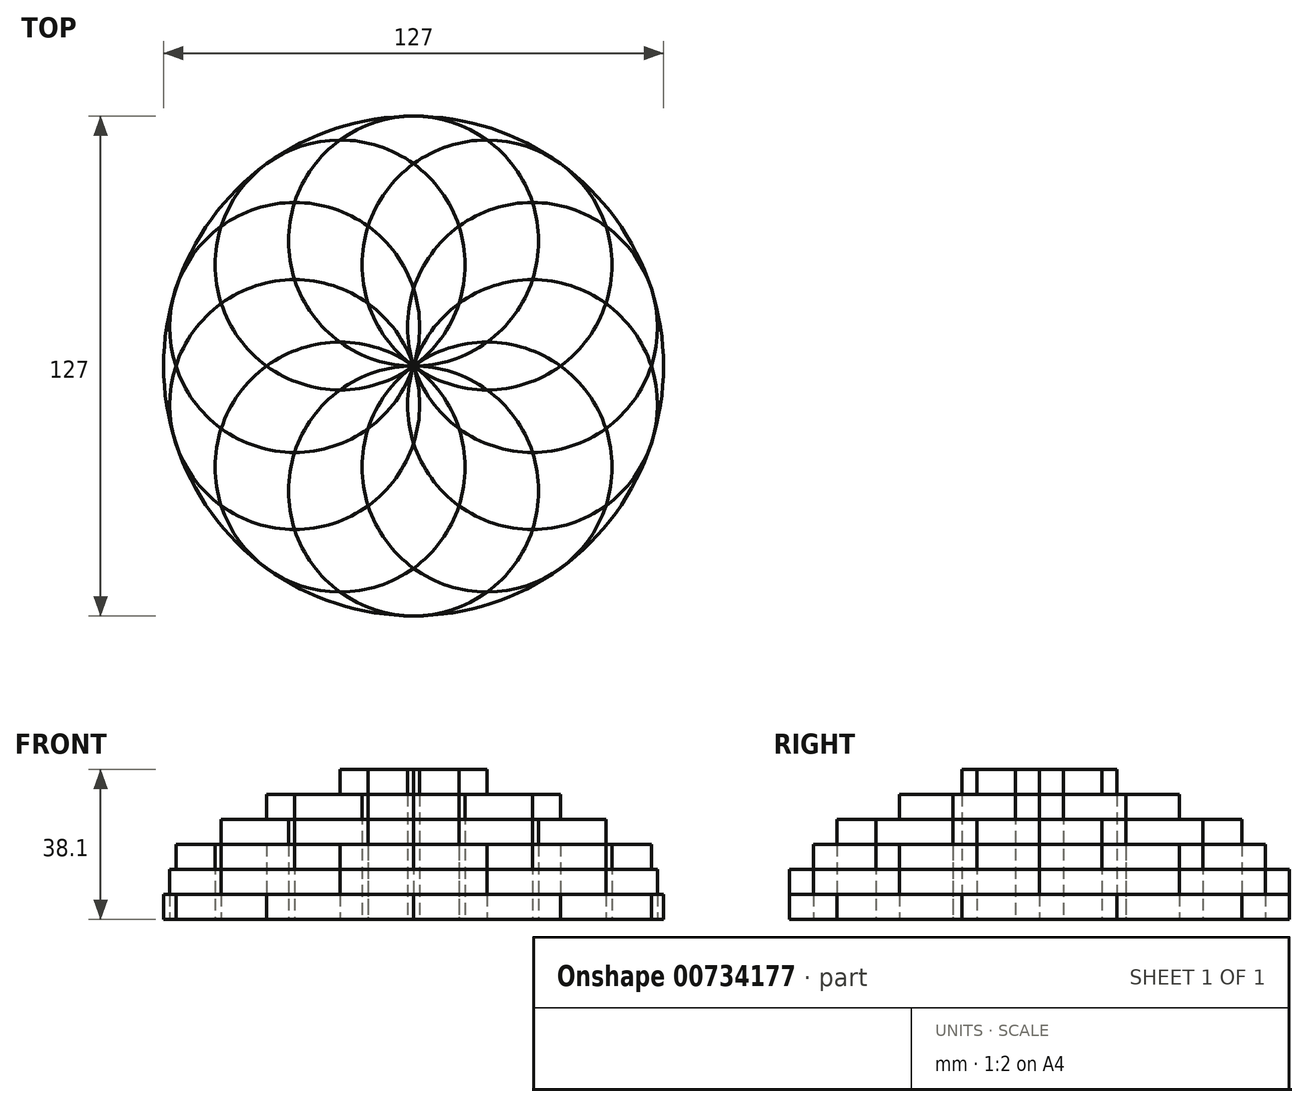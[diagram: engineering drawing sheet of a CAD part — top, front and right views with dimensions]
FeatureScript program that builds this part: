
annotation { "Feature Type Name" : "Feature", "Feature Type Description" : "" }
export const myFeature = defineFeature(function(context is Context, id is Id, definition is map)
    precondition{}
    {
        {
            var Q0;
            Q0=qCreatedBy(makeId("Top.planeOp"),FACE);
            var sketch = newSketch(context, id + "F0", { "sketchPlane" : qUnion([Q0])});
            skCircle(sketch, "E0", {"center": v(0, 0) * mm, "radius": 63.5 * mm});
            skCircle(sketch, "E1", {"center": v(0, 31.75) * mm, "radius": 31.75 * mm});
            skCircle(sketch, "E2.1.0", {"center": v(-18.66, 25.69) * mm, "radius": 31.75 * mm});
            skCircle(sketch, "E2.2.0", {"center": v(-30.2, 9.81) * mm, "radius": 31.75 * mm});
            skCircle(sketch, "E2.3.0", {"center": v(-30.2, -9.81) * mm, "radius": 31.75 * mm});
            skCircle(sketch, "E2.4.0", {"center": v(-18.66, -25.69) * mm, "radius": 31.75 * mm});
            skCircle(sketch, "E2.5.0", {"center": v(0, -31.75) * mm, "radius": 31.75 * mm});
            skCircle(sketch, "E2.6.0", {"center": v(18.66, -25.69) * mm, "radius": 31.75 * mm});
            skCircle(sketch, "E2.7.0", {"center": v(30.2, -9.81) * mm, "radius": 31.75 * mm});
            skCircle(sketch, "E2.8.0", {"center": v(30.2, 9.81) * mm, "radius": 31.75 * mm});
            skCircle(sketch, "E2.9.0", {"center": v(18.66, 25.69) * mm, "radius": 31.75 * mm});
            skSolve(sketch);
        }
        {
            var Q0;
            {var subQ0=sQuery(id+"F0.wireOp",EDGE,"E1");var subQ1=sQuery(id+"F0.wireOp",EDGE,"E0");var subQ2=makeQuery(id+"F0.imprint","INTERSECT",VERTEX,{"derivedFrom":[subQ1,subQ0]});Q0=makeQuery(id+"F0.imprint","IMPRINT",FACE,{"disambiguationData":[TD([[makeQuery(id+"F0.imprint","IMPRINT",EDGE,{"disambiguationData":[TD([[subQ2,-1.0]])],"derivedFrom":subQ1}),1.0]])]});}
            var Q1;
            {var subQ0=sQuery(id+"F0.wireOp",EDGE,"E2.1.0");var subQ1=sQuery(id+"F0.wireOp",EDGE,"E0");var subQ2=makeQuery(id+"F0.imprint","INTERSECT",VERTEX,{"derivedFrom":[subQ1,subQ0]});Q1=makeQuery(id+"F0.imprint","IMPRINT",FACE,{"disambiguationData":[TD([[makeQuery(id+"F0.imprint","IMPRINT",EDGE,{"disambiguationData":[TD([[subQ2,-1.0]])],"derivedFrom":subQ1}),1.0]])]});}
            var Q2;
            {var subQ0=sQuery(id+"F0.wireOp",EDGE,"E2.2.0");var subQ1=sQuery(id+"F0.wireOp",EDGE,"E0");var subQ2=makeQuery(id+"F0.imprint","INTERSECT",VERTEX,{"derivedFrom":[subQ1,subQ0]});Q2=makeQuery(id+"F0.imprint","IMPRINT",FACE,{"disambiguationData":[TD([[makeQuery(id+"F0.imprint","IMPRINT",EDGE,{"disambiguationData":[TD([[subQ2,-1.0]])],"derivedFrom":subQ1}),1.0]])]});}
            var Q3;
            {var subQ0=sQuery(id+"F0.wireOp",EDGE,"E2.3.0");var subQ1=sQuery(id+"F0.wireOp",EDGE,"E0");var subQ2=makeQuery(id+"F0.imprint","INTERSECT",VERTEX,{"derivedFrom":[subQ1,subQ0]});Q3=makeQuery(id+"F0.imprint","IMPRINT",FACE,{"disambiguationData":[TD([[makeQuery(id+"F0.imprint","IMPRINT",EDGE,{"disambiguationData":[TD([[subQ2,-1.0]])],"derivedFrom":subQ1}),1.0]])]});}
            var Q4;
            {var subQ0=sQuery(id+"F0.wireOp",EDGE,"E2.4.0");var subQ1=sQuery(id+"F0.wireOp",EDGE,"E0");var subQ2=makeQuery(id+"F0.imprint","INTERSECT",VERTEX,{"derivedFrom":[subQ1,subQ0]});Q4=makeQuery(id+"F0.imprint","IMPRINT",FACE,{"disambiguationData":[TD([[makeQuery(id+"F0.imprint","IMPRINT",EDGE,{"disambiguationData":[TD([[subQ2,-1.0]])],"derivedFrom":subQ1}),1.0]])]});}
            var Q5;
            {var subQ0=sQuery(id+"F0.wireOp",EDGE,"E2.5.0");var subQ1=sQuery(id+"F0.wireOp",EDGE,"E0");var subQ2=makeQuery(id+"F0.imprint","INTERSECT",VERTEX,{"derivedFrom":[subQ1,subQ0]});Q5=makeQuery(id+"F0.imprint","IMPRINT",FACE,{"disambiguationData":[TD([[makeQuery(id+"F0.imprint","IMPRINT",EDGE,{"disambiguationData":[TD([[subQ2,-1.0]])],"derivedFrom":subQ1}),1.0]])]});}
            var Q6;
            {var subQ0=sQuery(id+"F0.wireOp",EDGE,"E2.6.0");var subQ1=sQuery(id+"F0.wireOp",EDGE,"E0");var subQ2=makeQuery(id+"F0.imprint","INTERSECT",VERTEX,{"derivedFrom":[subQ1,subQ0]});Q6=makeQuery(id+"F0.imprint","IMPRINT",FACE,{"disambiguationData":[TD([[makeQuery(id+"F0.imprint","IMPRINT",EDGE,{"disambiguationData":[TD([[subQ2,-1.0]])],"derivedFrom":subQ1}),1.0]])]});}
            var Q7;
            {var subQ0=sQuery(id+"F0.wireOp",EDGE,"E2.9.0");var subQ1=sQuery(id+"F0.wireOp",EDGE,"E0");var subQ2=makeQuery(id+"F0.imprint","INTERSECT",VERTEX,{"derivedFrom":[subQ1,subQ0]});Q7=makeQuery(id+"F0.imprint","IMPRINT",FACE,{"disambiguationData":[TD([[makeQuery(id+"F0.imprint","IMPRINT",EDGE,{"disambiguationData":[TD([[subQ2,-1.0]])],"derivedFrom":subQ1}),1.0]])]});}
            var Q8;
            {var subQ0=sQuery(id+"F0.wireOp",EDGE,"E2.9.0");var subQ1=sQuery(id+"F0.wireOp",EDGE,"E0");var subQ2=makeQuery(id+"F0.imprint","INTERSECT",VERTEX,{"derivedFrom":[subQ1,subQ0]});Q8=makeQuery(id+"F0.imprint","IMPRINT",FACE,{"disambiguationData":[TD([[makeQuery(id+"F0.imprint","IMPRINT",EDGE,{"disambiguationData":[TD([[subQ2,1.0]])],"derivedFrom":subQ1}),1.0]])]});}
            var Q9;
            {var subQ0=sQuery(id+"F0.wireOp",EDGE,"E2.8.0");var subQ1=sQuery(id+"F0.wireOp",EDGE,"E0");var subQ2=makeQuery(id+"F0.imprint","INTERSECT",VERTEX,{"derivedFrom":[subQ1,subQ0]});Q9=makeQuery(id+"F0.imprint","IMPRINT",FACE,{"disambiguationData":[TD([[makeQuery(id+"F0.imprint","IMPRINT",EDGE,{"disambiguationData":[TD([[subQ2,1.0]])],"derivedFrom":subQ1}),1.0]])]});}
            extrude(context, id + "F1", {"entities" : qUnion([Q0, Q1, Q2, Q3, Q4, Q5, Q6, Q7, Q8, Q9]), "depth" : 6.35 * mm, "offsetDistance" : 25.4 * mm});
        }
        {
            var Q0;
            {var subQ0=sQuery(id+"F0.wireOp",EDGE,"E2.1.0");var subQ1=sQuery(id+"F0.wireOp",EDGE,"E1");var subQ2=makeQuery(id+"F0.imprint","INTERSECT",VERTEX,{"derivedFrom":[subQ1,subQ0]});Q0=makeQuery(id+"F0.imprint","IMPRINT",FACE,{"disambiguationData":[TD([[makeQuery(id+"F0.imprint","IMPRINT",EDGE,{"disambiguationData":[TD([[subQ2,-1.0]])],"derivedFrom":subQ1}),-1.0]])]});}
            var Q1;
            {var subQ0=sQuery(id+"F0.wireOp",EDGE,"E1");var subQ1=makeQuery(id+"F0.imprint","INTERSECT",VERTEX,{"derivedFrom":[sQuery(id+"F0.wireOp",EDGE,"E0"),subQ0]});Q1=makeQuery(id+"F0.imprint","IMPRINT",FACE,{"disambiguationData":[TD([[makeQuery(id+"F0.imprint","IMPRINT",EDGE,{"disambiguationData":[TD([[subQ1,1.0]])],"derivedFrom":subQ0}),1.0]])]});}
            var Q2;
            {var subQ0=sQuery(id+"F0.wireOp",EDGE,"E2.9.0");var subQ1=sQuery(id+"F0.wireOp",EDGE,"E1");var subQ2=makeQuery(id+"F0.imprint","INTERSECT",VERTEX,{"derivedFrom":[subQ1,subQ0]});Q2=makeQuery(id+"F0.imprint","IMPRINT",FACE,{"disambiguationData":[TD([[makeQuery(id+"F0.imprint","IMPRINT",EDGE,{"disambiguationData":[TD([[subQ2,1.0]])],"derivedFrom":subQ1}),-1.0]])]});}
            var Q3;
            {var subQ0=sQuery(id+"F0.wireOp",EDGE,"E2.8.0");var subQ1=sQuery(id+"F0.wireOp",EDGE,"E2.7.0");var subQ2=makeQuery(id+"F0.imprint","INTERSECT",VERTEX,{"derivedFrom":[subQ1,subQ0]});Q3=makeQuery(id+"F0.imprint","IMPRINT",FACE,{"disambiguationData":[TD([[makeQuery(id+"F0.imprint","IMPRINT",EDGE,{"disambiguationData":[TD([[subQ2,-1.0]])],"derivedFrom":subQ1}),-1.0]])]});}
            var Q4;
            {var subQ0=sQuery(id+"F0.wireOp",EDGE,"E2.7.0");var subQ1=sQuery(id+"F0.wireOp",EDGE,"E2.6.0");var subQ2=makeQuery(id+"F0.imprint","INTERSECT",VERTEX,{"derivedFrom":[subQ1,subQ0]});Q4=makeQuery(id+"F0.imprint","IMPRINT",FACE,{"disambiguationData":[TD([[makeQuery(id+"F0.imprint","IMPRINT",EDGE,{"disambiguationData":[TD([[subQ2,-1.0]])],"derivedFrom":subQ1}),-1.0]])]});}
            var Q5;
            {var subQ0=sQuery(id+"F0.wireOp",EDGE,"E2.5.0");var subQ1=sQuery(id+"F0.wireOp",EDGE,"E2.4.0");var subQ2=makeQuery(id+"F0.imprint","INTERSECT",VERTEX,{"derivedFrom":[subQ1,subQ0]});Q5=makeQuery(id+"F0.imprint","IMPRINT",FACE,{"disambiguationData":[TD([[makeQuery(id+"F0.imprint","IMPRINT",EDGE,{"disambiguationData":[TD([[subQ2,-1.0]])],"derivedFrom":subQ1}),-1.0]])]});}
            var Q6;
            {var subQ0=sQuery(id+"F0.wireOp",EDGE,"E2.6.0");var subQ1=sQuery(id+"F0.wireOp",EDGE,"E2.5.0");var subQ2=makeQuery(id+"F0.imprint","INTERSECT",VERTEX,{"derivedFrom":[subQ1,subQ0]});Q6=makeQuery(id+"F0.imprint","IMPRINT",FACE,{"disambiguationData":[TD([[makeQuery(id+"F0.imprint","IMPRINT",EDGE,{"disambiguationData":[TD([[subQ2,-1.0]])],"derivedFrom":subQ1}),-1.0]])]});}
            var Q7;
            {var subQ0=sQuery(id+"F0.wireOp",EDGE,"E2.4.0");var subQ1=sQuery(id+"F0.wireOp",EDGE,"E2.3.0");var subQ2=makeQuery(id+"F0.imprint","INTERSECT",VERTEX,{"derivedFrom":[subQ1,subQ0]});Q7=makeQuery(id+"F0.imprint","IMPRINT",FACE,{"disambiguationData":[TD([[makeQuery(id+"F0.imprint","IMPRINT",EDGE,{"disambiguationData":[TD([[subQ2,-1.0]])],"derivedFrom":subQ1}),-1.0]])]});}
            var Q8;
            {var subQ0=sQuery(id+"F0.wireOp",EDGE,"E2.3.0");var subQ1=sQuery(id+"F0.wireOp",EDGE,"E2.2.0");var subQ2=makeQuery(id+"F0.imprint","INTERSECT",VERTEX,{"derivedFrom":[subQ1,subQ0]});Q8=makeQuery(id+"F0.imprint","IMPRINT",FACE,{"disambiguationData":[TD([[makeQuery(id+"F0.imprint","IMPRINT",EDGE,{"disambiguationData":[TD([[subQ2,-1.0]])],"derivedFrom":subQ1}),-1.0]])]});}
            var Q9;
            {var subQ0=sQuery(id+"F0.wireOp",EDGE,"E2.2.0");var subQ1=sQuery(id+"F0.wireOp",EDGE,"E2.1.0");var subQ2=makeQuery(id+"F0.imprint","INTERSECT",VERTEX,{"derivedFrom":[subQ1,subQ0]});Q9=makeQuery(id+"F0.imprint","IMPRINT",FACE,{"disambiguationData":[TD([[makeQuery(id+"F0.imprint","IMPRINT",EDGE,{"disambiguationData":[TD([[subQ2,-1.0]])],"derivedFrom":subQ1}),-1.0]])]});}
            extrude(context, id + "F2", {"entities" : qUnion([Q0, Q1, Q2, Q3, Q4, Q5, Q6, Q7, Q8, Q9]), "depth" : 12.7 * mm, "offsetDistance" : 25.4 * mm});
        }
        {
            var Q0;
            {var subQ0=sQuery(id+"F0.wireOp",EDGE,"E2.9.0");var subQ1=sQuery(id+"F0.wireOp",EDGE,"E1");var subQ2=makeQuery(id+"F0.imprint","INTERSECT",VERTEX,{"derivedFrom":[subQ1,subQ0]});Q0=makeQuery(id+"F0.imprint","IMPRINT",FACE,{"disambiguationData":[TD([[makeQuery(id+"F0.imprint","IMPRINT",EDGE,{"disambiguationData":[TD([[subQ2,1.0]])],"derivedFrom":subQ1}),1.0]])]});}
            var Q1;
            {var subQ0=sQuery(id+"F0.wireOp",EDGE,"E2.1.0");var subQ1=sQuery(id+"F0.wireOp",EDGE,"E1");var subQ2=makeQuery(id+"F0.imprint","INTERSECT",VERTEX,{"derivedFrom":[subQ1,subQ0]});Q1=makeQuery(id+"F0.imprint","IMPRINT",FACE,{"disambiguationData":[TD([[makeQuery(id+"F0.imprint","IMPRINT",EDGE,{"disambiguationData":[TD([[subQ2,-1.0]])],"derivedFrom":subQ1}),1.0]])]});}
            var Q2;
            {var subQ0=sQuery(id+"F0.wireOp",EDGE,"E2.2.0");var subQ1=sQuery(id+"F0.wireOp",EDGE,"E1");var subQ2=makeQuery(id+"F0.imprint","INTERSECT",VERTEX,{"derivedFrom":[subQ1,subQ0]});Q2=makeQuery(id+"F0.imprint","IMPRINT",FACE,{"disambiguationData":[TD([[makeQuery(id+"F0.imprint","IMPRINT",EDGE,{"disambiguationData":[TD([[subQ2,-1.0]])],"derivedFrom":subQ1}),-1.0]])]});}
            var Q3;
            {var subQ0=sQuery(id+"F0.wireOp",EDGE,"E2.3.0");var subQ1=sQuery(id+"F0.wireOp",EDGE,"E2.1.0");var subQ2=makeQuery(id+"F0.imprint","INTERSECT",VERTEX,{"derivedFrom":[subQ1,subQ0]});Q3=makeQuery(id+"F0.imprint","IMPRINT",FACE,{"disambiguationData":[TD([[makeQuery(id+"F0.imprint","IMPRINT",EDGE,{"disambiguationData":[TD([[subQ2,-1.0]])],"derivedFrom":subQ1}),-1.0]])]});}
            var Q4;
            {var subQ0=sQuery(id+"F0.wireOp",EDGE,"E2.4.0");var subQ1=sQuery(id+"F0.wireOp",EDGE,"E2.2.0");var subQ2=makeQuery(id+"F0.imprint","INTERSECT",VERTEX,{"derivedFrom":[subQ1,subQ0]});Q4=makeQuery(id+"F0.imprint","IMPRINT",FACE,{"disambiguationData":[TD([[makeQuery(id+"F0.imprint","IMPRINT",EDGE,{"disambiguationData":[TD([[subQ2,-1.0]])],"derivedFrom":subQ1}),-1.0]])]});}
            var Q5;
            {var subQ0=sQuery(id+"F0.wireOp",EDGE,"E2.5.0");var subQ1=sQuery(id+"F0.wireOp",EDGE,"E2.3.0");var subQ2=makeQuery(id+"F0.imprint","INTERSECT",VERTEX,{"derivedFrom":[subQ1,subQ0]});Q5=makeQuery(id+"F0.imprint","IMPRINT",FACE,{"disambiguationData":[TD([[makeQuery(id+"F0.imprint","IMPRINT",EDGE,{"disambiguationData":[TD([[subQ2,-1.0]])],"derivedFrom":subQ1}),-1.0]])]});}
            var Q6;
            {var subQ0=sQuery(id+"F0.wireOp",EDGE,"E2.6.0");var subQ1=sQuery(id+"F0.wireOp",EDGE,"E2.4.0");var subQ2=makeQuery(id+"F0.imprint","INTERSECT",VERTEX,{"derivedFrom":[subQ1,subQ0]});Q6=makeQuery(id+"F0.imprint","IMPRINT",FACE,{"disambiguationData":[TD([[makeQuery(id+"F0.imprint","IMPRINT",EDGE,{"disambiguationData":[TD([[subQ2,-1.0]])],"derivedFrom":subQ1}),-1.0]])]});}
            var Q7;
            {var subQ0=sQuery(id+"F0.wireOp",EDGE,"E2.7.0");var subQ1=sQuery(id+"F0.wireOp",EDGE,"E2.5.0");var subQ2=makeQuery(id+"F0.imprint","INTERSECT",VERTEX,{"derivedFrom":[subQ1,subQ0]});Q7=makeQuery(id+"F0.imprint","IMPRINT",FACE,{"disambiguationData":[TD([[makeQuery(id+"F0.imprint","IMPRINT",EDGE,{"disambiguationData":[TD([[subQ2,-1.0]])],"derivedFrom":subQ1}),-1.0]])]});}
            var Q8;
            {var subQ0=sQuery(id+"F0.wireOp",EDGE,"E2.8.0");var subQ1=sQuery(id+"F0.wireOp",EDGE,"E2.6.0");var subQ2=makeQuery(id+"F0.imprint","INTERSECT",VERTEX,{"derivedFrom":[subQ1,subQ0]});Q8=makeQuery(id+"F0.imprint","IMPRINT",FACE,{"disambiguationData":[TD([[makeQuery(id+"F0.imprint","IMPRINT",EDGE,{"disambiguationData":[TD([[subQ2,-1.0]])],"derivedFrom":subQ1}),-1.0]])]});}
            var Q9;
            {var subQ0=sQuery(id+"F0.wireOp",EDGE,"E2.8.0");var subQ1=sQuery(id+"F0.wireOp",EDGE,"E1");var subQ2=makeQuery(id+"F0.imprint","INTERSECT",VERTEX,{"derivedFrom":[subQ1,subQ0]});Q9=makeQuery(id+"F0.imprint","IMPRINT",FACE,{"disambiguationData":[TD([[makeQuery(id+"F0.imprint","IMPRINT",EDGE,{"disambiguationData":[TD([[subQ2,1.0]])],"derivedFrom":subQ1}),-1.0]])]});}
            extrude(context, id + "F3", {"entities" : qUnion([Q0, Q1, Q2, Q3, Q4, Q5, Q6, Q7, Q8, Q9]), "depth" : 19.05 * mm, "offsetDistance" : 25.4 * mm});
        }
        {
            var Q0;
            {var subQ0=sQuery(id+"F0.wireOp",EDGE,"E2.8.0");var subQ1=sQuery(id+"F0.wireOp",EDGE,"E1");var subQ2=makeQuery(id+"F0.imprint","INTERSECT",VERTEX,{"derivedFrom":[subQ1,subQ0]});Q0=makeQuery(id+"F0.imprint","IMPRINT",FACE,{"disambiguationData":[TD([[makeQuery(id+"F0.imprint","IMPRINT",EDGE,{"disambiguationData":[TD([[subQ2,1.0]])],"derivedFrom":subQ1}),1.0]])]});}
            var Q1;
            {var subQ0=sQuery(id+"F0.wireOp",EDGE,"E2.9.0");var subQ1=sQuery(id+"F0.wireOp",EDGE,"E2.1.0");var subQ2=makeQuery(id+"F0.imprint","INTERSECT",VERTEX,{"derivedFrom":[subQ1,subQ0]});Q1=makeQuery(id+"F0.imprint","IMPRINT",FACE,{"disambiguationData":[TD([[makeQuery(id+"F0.imprint","IMPRINT",EDGE,{"disambiguationData":[TD([[subQ2,1.0]])],"derivedFrom":subQ1}),1.0]])]});}
            var Q2;
            {var subQ0=sQuery(id+"F0.wireOp",EDGE,"E2.2.0");var subQ1=sQuery(id+"F0.wireOp",EDGE,"E1");var subQ2=makeQuery(id+"F0.imprint","INTERSECT",VERTEX,{"derivedFrom":[subQ1,subQ0]});Q2=makeQuery(id+"F0.imprint","IMPRINT",FACE,{"disambiguationData":[TD([[makeQuery(id+"F0.imprint","IMPRINT",EDGE,{"disambiguationData":[TD([[subQ2,-1.0]])],"derivedFrom":subQ1}),1.0]])]});}
            var Q3;
            {var subQ0=sQuery(id+"F0.wireOp",EDGE,"E2.3.0");var subQ1=sQuery(id+"F0.wireOp",EDGE,"E1");var subQ2=makeQuery(id+"F0.imprint","INTERSECT",VERTEX,{"derivedFrom":[subQ1,subQ0]});Q3=makeQuery(id+"F0.imprint","IMPRINT",FACE,{"disambiguationData":[TD([[makeQuery(id+"F0.imprint","IMPRINT",EDGE,{"disambiguationData":[TD([[subQ2,-1.0]])],"derivedFrom":subQ1}),-1.0]])]});}
            var Q4;
            {var subQ0=sQuery(id+"F0.wireOp",EDGE,"E2.4.0");var subQ1=sQuery(id+"F0.wireOp",EDGE,"E2.1.0");var subQ2=makeQuery(id+"F0.imprint","INTERSECT",VERTEX,{"derivedFrom":[subQ1,subQ0]});Q4=makeQuery(id+"F0.imprint","IMPRINT",FACE,{"disambiguationData":[TD([[makeQuery(id+"F0.imprint","IMPRINT",EDGE,{"disambiguationData":[TD([[subQ2,-1.0]])],"derivedFrom":subQ1}),-1.0]])]});}
            var Q5;
            {var subQ0=sQuery(id+"F0.wireOp",EDGE,"E2.5.0");var subQ1=sQuery(id+"F0.wireOp",EDGE,"E2.2.0");var subQ2=makeQuery(id+"F0.imprint","INTERSECT",VERTEX,{"derivedFrom":[subQ1,subQ0]});Q5=makeQuery(id+"F0.imprint","IMPRINT",FACE,{"disambiguationData":[TD([[makeQuery(id+"F0.imprint","IMPRINT",EDGE,{"disambiguationData":[TD([[subQ2,-1.0]])],"derivedFrom":subQ1}),-1.0]])]});}
            var Q6;
            {var subQ0=sQuery(id+"F0.wireOp",EDGE,"E2.6.0");var subQ1=sQuery(id+"F0.wireOp",EDGE,"E2.3.0");var subQ2=makeQuery(id+"F0.imprint","INTERSECT",VERTEX,{"derivedFrom":[subQ1,subQ0]});Q6=makeQuery(id+"F0.imprint","IMPRINT",FACE,{"disambiguationData":[TD([[makeQuery(id+"F0.imprint","IMPRINT",EDGE,{"disambiguationData":[TD([[subQ2,-1.0]])],"derivedFrom":subQ1}),-1.0]])]});}
            var Q7;
            {var subQ0=sQuery(id+"F0.wireOp",EDGE,"E2.7.0");var subQ1=sQuery(id+"F0.wireOp",EDGE,"E2.4.0");var subQ2=makeQuery(id+"F0.imprint","INTERSECT",VERTEX,{"derivedFrom":[subQ1,subQ0]});Q7=makeQuery(id+"F0.imprint","IMPRINT",FACE,{"disambiguationData":[TD([[makeQuery(id+"F0.imprint","IMPRINT",EDGE,{"disambiguationData":[TD([[subQ2,-1.0]])],"derivedFrom":subQ1}),-1.0]])]});}
            var Q8;
            {var subQ0=sQuery(id+"F0.wireOp",EDGE,"E2.8.0");var subQ1=sQuery(id+"F0.wireOp",EDGE,"E2.5.0");var subQ2=makeQuery(id+"F0.imprint","INTERSECT",VERTEX,{"derivedFrom":[subQ1,subQ0]});Q8=makeQuery(id+"F0.imprint","IMPRINT",FACE,{"disambiguationData":[TD([[makeQuery(id+"F0.imprint","IMPRINT",EDGE,{"disambiguationData":[TD([[subQ2,-1.0]])],"derivedFrom":subQ1}),-1.0]])]});}
            var Q9;
            {var subQ0=sQuery(id+"F0.wireOp",EDGE,"E2.6.0");var subQ1=sQuery(id+"F0.wireOp",EDGE,"E1");var subQ2=makeQuery(id+"F0.imprint","INTERSECT",VERTEX,{"derivedFrom":[subQ1,subQ0]});Q9=makeQuery(id+"F0.imprint","IMPRINT",FACE,{"disambiguationData":[TD([[makeQuery(id+"F0.imprint","IMPRINT",EDGE,{"disambiguationData":[TD([[subQ2,-1.0]])],"derivedFrom":subQ1}),-1.0]])]});}
            extrude(context, id + "F4", {"entities" : qUnion([Q0, Q1, Q2, Q3, Q4, Q5, Q6, Q7, Q8, Q9]), "depth" : 25.4 * mm, "offsetDistance" : 25.4 * mm});
        }
        {
            var Q0;
            {var subQ0=sQuery(id+"F0.wireOp",EDGE,"E2.3.0");var subQ1=sQuery(id+"F0.wireOp",EDGE,"E1");var subQ2=makeQuery(id+"F0.imprint","INTERSECT",VERTEX,{"derivedFrom":[subQ1,subQ0]});Q0=makeQuery(id+"F0.imprint","IMPRINT",FACE,{"disambiguationData":[TD([[makeQuery(id+"F0.imprint","IMPRINT",EDGE,{"disambiguationData":[TD([[subQ2,-1.0]])],"derivedFrom":subQ1}),1.0]])]});}
            var Q1;
            {var subQ0=sQuery(id+"F0.wireOp",EDGE,"E2.4.0");var subQ4=sQuery(id+"F0.wireOp",EDGE,"E2.1.0");var subQ6=makeQuery(id+"F0.imprint","INTERSECT",VERTEX,{"derivedFrom":[subQ4,subQ0]});Q1=makeQuery(id+"F0.imprint","IMPRINT",FACE,{"disambiguationData":[TD([[makeQuery(id+"F0.imprint","IMPRINT",EDGE,{"disambiguationData":[TD([[subQ6,-1.0]])],"derivedFrom":subQ4}),1.0]])]});}
            var Q2;
            {var subQ0=sQuery(id+"F0.wireOp",EDGE,"E2.5.0");var subQ4=sQuery(id+"F0.wireOp",EDGE,"E2.2.0");var subQ6=makeQuery(id+"F0.imprint","INTERSECT",VERTEX,{"derivedFrom":[subQ4,subQ0]});Q2=makeQuery(id+"F0.imprint","IMPRINT",FACE,{"disambiguationData":[TD([[makeQuery(id+"F0.imprint","IMPRINT",EDGE,{"disambiguationData":[TD([[subQ6,-1.0]])],"derivedFrom":subQ4}),1.0]])]});}
            var Q3;
            {var subQ0=sQuery(id+"F0.wireOp",EDGE,"E2.6.0");var subQ4=sQuery(id+"F0.wireOp",EDGE,"E2.3.0");var subQ6=makeQuery(id+"F0.imprint","INTERSECT",VERTEX,{"derivedFrom":[subQ4,subQ0]});Q3=makeQuery(id+"F0.imprint","IMPRINT",FACE,{"disambiguationData":[TD([[makeQuery(id+"F0.imprint","IMPRINT",EDGE,{"disambiguationData":[TD([[subQ6,-1.0]])],"derivedFrom":subQ4}),1.0]])]});}
            var Q4;
            {var subQ0=sQuery(id+"F0.wireOp",EDGE,"E2.7.0");var subQ4=sQuery(id+"F0.wireOp",EDGE,"E2.4.0");var subQ6=makeQuery(id+"F0.imprint","INTERSECT",VERTEX,{"derivedFrom":[subQ4,subQ0]});Q4=makeQuery(id+"F0.imprint","IMPRINT",FACE,{"disambiguationData":[TD([[makeQuery(id+"F0.imprint","IMPRINT",EDGE,{"disambiguationData":[TD([[subQ6,-1.0]])],"derivedFrom":subQ4}),1.0]])]});}
            var Q5;
            {var subQ0=sQuery(id+"F0.wireOp",EDGE,"E2.8.0");var subQ4=sQuery(id+"F0.wireOp",EDGE,"E2.5.0");var subQ6=makeQuery(id+"F0.imprint","INTERSECT",VERTEX,{"derivedFrom":[subQ4,subQ0]});Q5=makeQuery(id+"F0.imprint","IMPRINT",FACE,{"disambiguationData":[TD([[makeQuery(id+"F0.imprint","IMPRINT",EDGE,{"disambiguationData":[TD([[subQ6,-1.0]])],"derivedFrom":subQ4}),1.0]])]});}
            var Q6;
            {var subQ0=sQuery(id+"F0.wireOp",EDGE,"E2.6.0");var subQ1=sQuery(id+"F0.wireOp",EDGE,"E1");var subQ2=makeQuery(id+"F0.imprint","INTERSECT",VERTEX,{"derivedFrom":[subQ1,subQ0]});Q6=makeQuery(id+"F0.imprint","IMPRINT",FACE,{"disambiguationData":[TD([[makeQuery(id+"F0.imprint","IMPRINT",EDGE,{"disambiguationData":[TD([[subQ2,1.0]])],"derivedFrom":subQ0}),1.0]])]});}
            var Q7;
            {var subQ0=sQuery(id+"F0.wireOp",EDGE,"E2.6.0");var subQ1=sQuery(id+"F0.wireOp",EDGE,"E1");var subQ2=makeQuery(id+"F0.imprint","INTERSECT",VERTEX,{"derivedFrom":[subQ1,subQ0]});Q7=makeQuery(id+"F0.imprint","IMPRINT",FACE,{"disambiguationData":[TD([[makeQuery(id+"F0.imprint","IMPRINT",EDGE,{"disambiguationData":[TD([[subQ2,-1.0]])],"derivedFrom":subQ1}),1.0]])]});}
            var Q8;
            {var subQ0=sQuery(id+"F0.wireOp",EDGE,"E2.7.0");var subQ1=sQuery(id+"F0.wireOp",EDGE,"E2.1.0");var subQ2=makeQuery(id+"F0.imprint","INTERSECT",VERTEX,{"derivedFrom":[subQ1,subQ0]});Q8=makeQuery(id+"F0.imprint","IMPRINT",FACE,{"disambiguationData":[TD([[makeQuery(id+"F0.imprint","IMPRINT",EDGE,{"disambiguationData":[TD([[subQ2,-1.0]])],"derivedFrom":subQ1}),1.0]])]});}
            var Q9;
            {var subQ0=sQuery(id+"F0.wireOp",EDGE,"E2.8.0");var subQ1=sQuery(id+"F0.wireOp",EDGE,"E2.2.0");var subQ2=makeQuery(id+"F0.imprint","INTERSECT",VERTEX,{"derivedFrom":[subQ1,subQ0]});Q9=makeQuery(id+"F0.imprint","IMPRINT",FACE,{"disambiguationData":[TD([[makeQuery(id+"F0.imprint","IMPRINT",EDGE,{"disambiguationData":[TD([[subQ2,-1.0]])],"derivedFrom":subQ1}),1.0]])]});}
            extrude(context, id + "F5", {"entities" : qUnion([Q0, Q1, Q2, Q3, Q4, Q5, Q6, Q7, Q8, Q9]), "depth" : 31.75 * mm, "offsetDistance" : 25.4 * mm});
        }
        {
            var Q0;
            {var subQ0=sQuery(id+"F0.wireOp",EDGE,"E2.9.0");var subQ1=sQuery(id+"F0.wireOp",EDGE,"E2.3.0");var subQ2=makeQuery(id+"F0.imprint","INTERSECT",VERTEX,{"derivedFrom":[subQ1,subQ0]});Q0=makeQuery(id+"F0.imprint","IMPRINT",FACE,{"disambiguationData":[TD([[makeQuery(id+"F0.imprint","IMPRINT",EDGE,{"disambiguationData":[TD([[subQ2,1.0]])],"derivedFrom":subQ1}),1.0]])]});}
            var Q1;
            {var subQ0=sQuery(id+"F0.wireOp",EDGE,"E2.8.0");var subQ1=sQuery(id+"F0.wireOp",EDGE,"E2.2.0");var subQ2=makeQuery(id+"F0.imprint","INTERSECT",VERTEX,{"derivedFrom":[subQ1,subQ0]});Q1=makeQuery(id+"F0.imprint","IMPRINT",FACE,{"disambiguationData":[TD([[makeQuery(id+"F0.imprint","IMPRINT",EDGE,{"disambiguationData":[TD([[subQ2,1.0]])],"derivedFrom":subQ1}),1.0]])]});}
            var Q2;
            {var subQ0=sQuery(id+"F0.wireOp",EDGE,"E2.7.0");var subQ1=sQuery(id+"F0.wireOp",EDGE,"E2.1.0");var subQ2=makeQuery(id+"F0.imprint","INTERSECT",VERTEX,{"derivedFrom":[subQ1,subQ0]});Q2=makeQuery(id+"F0.imprint","IMPRINT",FACE,{"disambiguationData":[TD([[makeQuery(id+"F0.imprint","IMPRINT",EDGE,{"disambiguationData":[TD([[subQ2,1.0]])],"derivedFrom":subQ1}),1.0]])]});}
            var Q3;
            {var subQ0=sQuery(id+"F0.wireOp",EDGE,"E2.6.0");var subQ1=sQuery(id+"F0.wireOp",EDGE,"E1");var subQ2=makeQuery(id+"F0.imprint","INTERSECT",VERTEX,{"derivedFrom":[subQ1,subQ0]});Q3=makeQuery(id+"F0.imprint","IMPRINT",FACE,{"disambiguationData":[TD([[makeQuery(id+"F0.imprint","IMPRINT",EDGE,{"disambiguationData":[TD([[subQ2,1.0]])],"derivedFrom":subQ1}),1.0]])]});}
            var Q4;
            {var subQ0=sQuery(id+"F0.wireOp",EDGE,"E2.9.0");var subQ1=sQuery(id+"F0.wireOp",EDGE,"E2.5.0");var subQ2=makeQuery(id+"F0.imprint","INTERSECT",VERTEX,{"derivedFrom":[subQ1,subQ0]});Q4=makeQuery(id+"F0.imprint","IMPRINT",FACE,{"disambiguationData":[TD([[makeQuery(id+"F0.imprint","IMPRINT",EDGE,{"disambiguationData":[TD([[subQ2,-1.0]])],"derivedFrom":subQ1}),1.0]])]});}
            var Q5;
            {var subQ0=sQuery(id+"F0.wireOp",EDGE,"E2.8.0");var subQ1=sQuery(id+"F0.wireOp",EDGE,"E2.4.0");var subQ2=makeQuery(id+"F0.imprint","INTERSECT",VERTEX,{"derivedFrom":[subQ1,subQ0]});Q5=makeQuery(id+"F0.imprint","IMPRINT",FACE,{"disambiguationData":[TD([[makeQuery(id+"F0.imprint","IMPRINT",EDGE,{"disambiguationData":[TD([[subQ2,-1.0]])],"derivedFrom":subQ1}),1.0]])]});}
            var Q6;
            {var subQ0=sQuery(id+"F0.wireOp",EDGE,"E2.7.0");var subQ1=sQuery(id+"F0.wireOp",EDGE,"E2.3.0");var subQ2=makeQuery(id+"F0.imprint","INTERSECT",VERTEX,{"derivedFrom":[subQ1,subQ0]});Q6=makeQuery(id+"F0.imprint","IMPRINT",FACE,{"disambiguationData":[TD([[makeQuery(id+"F0.imprint","IMPRINT",EDGE,{"disambiguationData":[TD([[subQ2,-1.0]])],"derivedFrom":subQ1}),1.0]])]});}
            var Q7;
            {var subQ0=sQuery(id+"F0.wireOp",EDGE,"E2.6.0");var subQ1=sQuery(id+"F0.wireOp",EDGE,"E2.2.0");var subQ2=makeQuery(id+"F0.imprint","INTERSECT",VERTEX,{"derivedFrom":[subQ1,subQ0]});Q7=makeQuery(id+"F0.imprint","IMPRINT",FACE,{"disambiguationData":[TD([[makeQuery(id+"F0.imprint","IMPRINT",EDGE,{"disambiguationData":[TD([[subQ2,-1.0]])],"derivedFrom":subQ1}),1.0]])]});}
            var Q8;
            {var subQ0=sQuery(id+"F0.wireOp",EDGE,"E2.5.0");var subQ1=sQuery(id+"F0.wireOp",EDGE,"E2.1.0");var subQ2=makeQuery(id+"F0.imprint","INTERSECT",VERTEX,{"derivedFrom":[subQ1,subQ0]});Q8=makeQuery(id+"F0.imprint","IMPRINT",FACE,{"disambiguationData":[TD([[makeQuery(id+"F0.imprint","IMPRINT",EDGE,{"disambiguationData":[TD([[subQ2,-1.0]])],"derivedFrom":subQ1}),1.0]])]});}
            var Q9;
            {var subQ0=sQuery(id+"F0.wireOp",EDGE,"E2.4.0");var subQ1=sQuery(id+"F0.wireOp",EDGE,"E1");var subQ2=makeQuery(id+"F0.imprint","INTERSECT",VERTEX,{"derivedFrom":[subQ1,subQ0]});Q9=makeQuery(id+"F0.imprint","IMPRINT",FACE,{"disambiguationData":[TD([[makeQuery(id+"F0.imprint","IMPRINT",EDGE,{"disambiguationData":[TD([[subQ2,-1.0]])],"derivedFrom":subQ1}),1.0]])]});}
            extrude(context, id + "F6", {"entities" : qUnion([Q0, Q1, Q2, Q3, Q4, Q5, Q6, Q7, Q8, Q9]), "depth" : 38.1 * mm, "offsetDistance" : 25.4 * mm});
        }
    });
